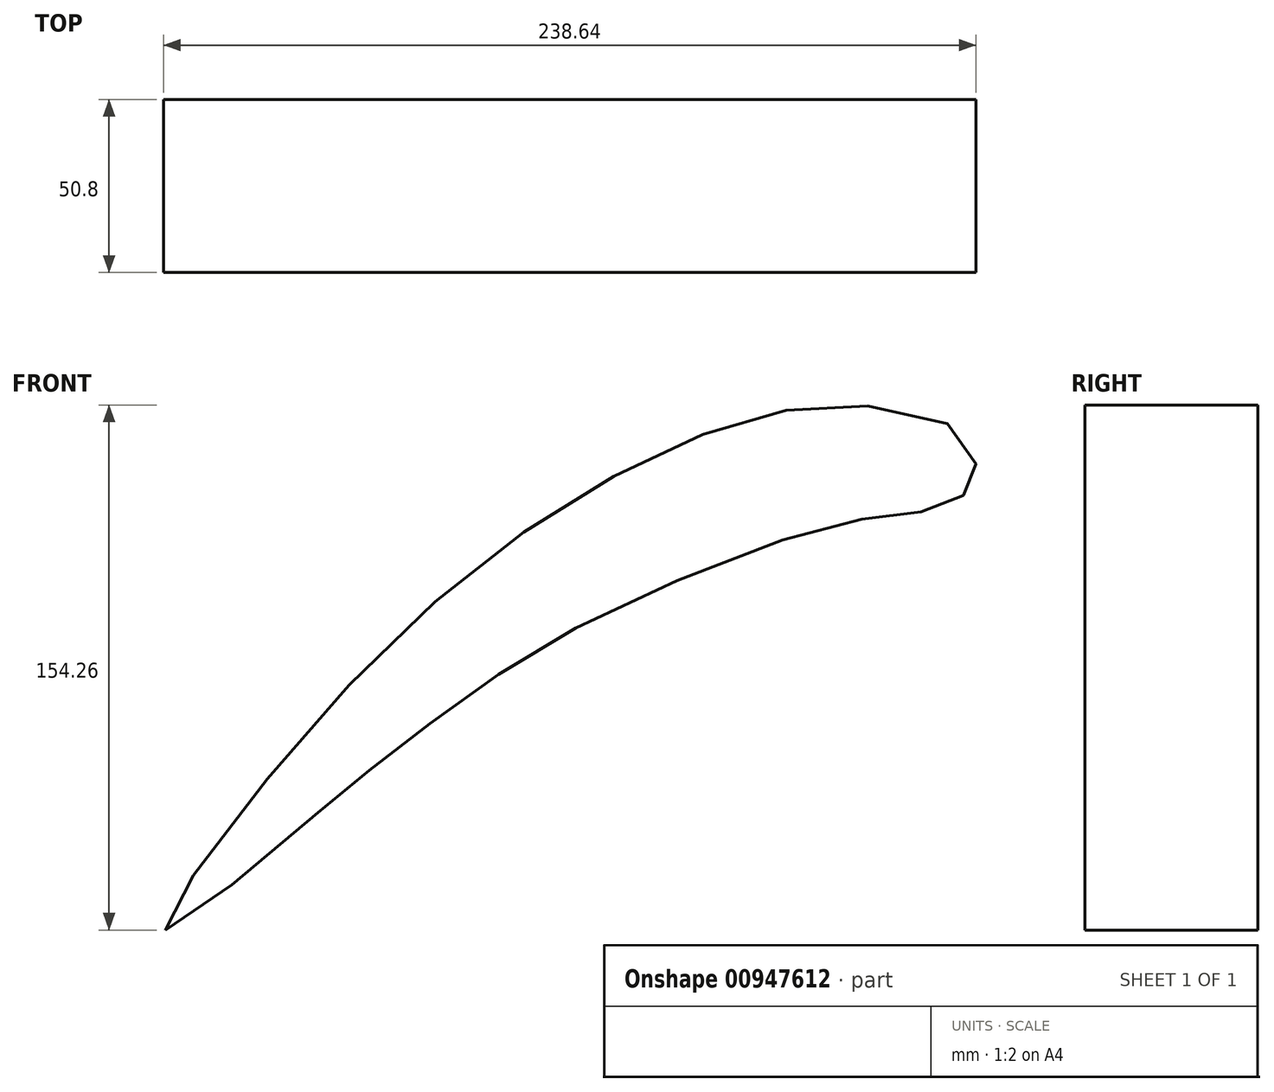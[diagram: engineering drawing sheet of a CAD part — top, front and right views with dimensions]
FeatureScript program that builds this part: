
annotation { "Feature Type Name" : "Feature", "Feature Type Description" : "" }
export const myFeature = defineFeature(function(context is Context, id is Id, definition is map)
    precondition{}
    {
        {
            var Q0;
            Q0=qCreatedBy(makeId("Front.planeOp"),FACE);
            var sketch = newSketch(context, id + "F0", { "sketchPlane" : qUnion([Q0])});
            skFitSpline(sketch, "E0", {"points": [v(0, 0) * mm, v(17, 28) * mm, v(71, 89) * mm, v(124, 129) * mm, v(170, 149.81) * mm, v(206, 154) * mm, v(235, 145.17) * mm, v(238, 135) * mm, v(236, 129.5) * mm, v(229, 124.5) * mm, v(214, 122) * mm, v(187, 116.4) * mm, v(125, 91) * mm, v(88.5, 68.64) * mm, v(61, 47.81) * mm, v(40, 30.5) * mm, v(0, 0) * mm]});
            skSolve(sketch);
        }
        {
            var Q0;
            Q0 = qSketchRegion(id + "F0", true);
            extrude(context, id + "F1", {"entities" : qUnion([Q0]), "depth" : 50.8 * mm, "offsetDistance" : 25.4 * mm});
        }
    });
